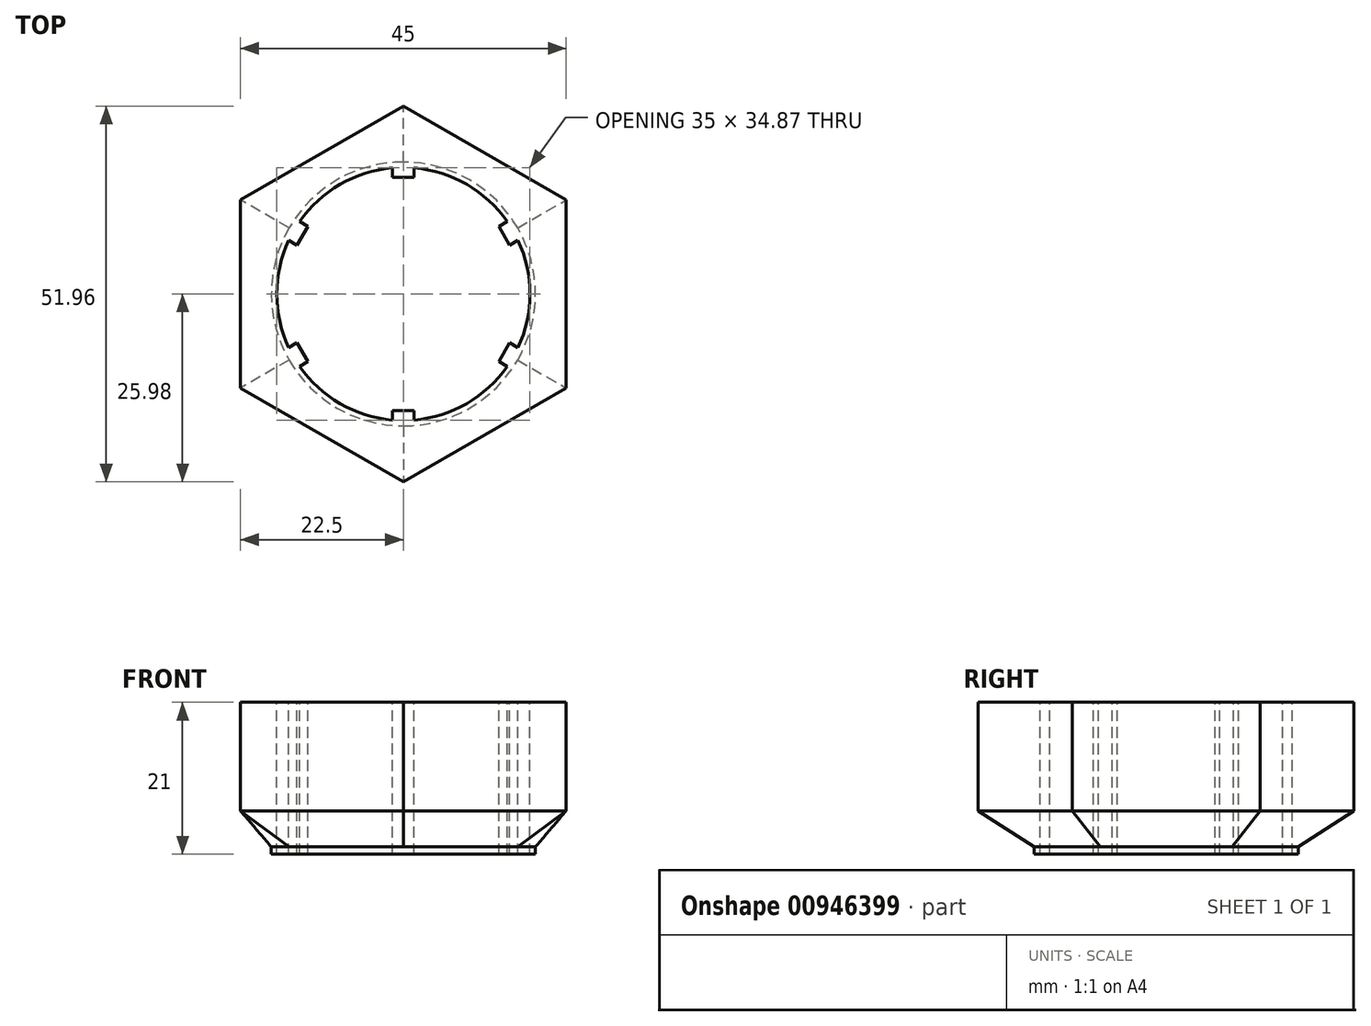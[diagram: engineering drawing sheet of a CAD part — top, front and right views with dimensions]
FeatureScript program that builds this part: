
annotation { "Feature Type Name" : "Feature", "Feature Type Description" : "" }
export const myFeature = defineFeature(function(context is Context, id is Id, definition is map)
    precondition{}
    {
        {
            var Q0;
            Q0=qCreatedBy(makeId("Top.planeOp"),FACE);
            var sketch = newSketch(context, id + "F0", { "sketchPlane" : qUnion([Q0])});
            skCircle(sketch, "E0", {"center": v(0, 0) * mm, "radius": 18.25 * mm});
            skArc(sketch, "E1", {"start": v(-15.85, 7.42) * mm, "mid": v(-17.5, 0) * mm, "end": v(-15.85, -7.42) * mm, "construction": true});
            skCircle(sketch, "E2", {"center": v(0, 0) * mm, "radius": 16.1 * mm, "construction": true});
            skLineSegment(sketch, "E3", {"start": v(0, 16.1) * mm, "end": v(0, 17.5) * mm, "construction": true});
            skLineSegment(sketch, "E4", {"start": v(-1.5, 16.1) * mm, "end": v(1.5, 16.1) * mm, "construction": true});
            skLineSegment(sketch, "E5", {"start": v(1.5, 16.1) * mm, "end": v(1.5, 17.44) * mm, "construction": true});
            skLineSegment(sketch, "E6", {"start": v(-1.5, 16.1) * mm, "end": v(-1.5, 17.44) * mm, "construction": true});
            skLineSegment(sketch, "E7.1.0", {"start": v(-14.7, 6.75) * mm, "end": v(-15.85, 7.42) * mm, "construction": true});
            skLineSegment(sketch, "E7.1.1", {"start": v(-13.2, 9.35) * mm, "end": v(-14.35, 10.02) * mm, "construction": true});
            skLineSegment(sketch, "E7.1.2", {"start": v(-14.7, 6.75) * mm, "end": v(-13.2, 9.35) * mm, "construction": true});
            skLineSegment(sketch, "E7.2.0", {"start": v(-13.2, -9.35) * mm, "end": v(-14.35, -10.02) * mm, "construction": true});
            skLineSegment(sketch, "E7.2.1", {"start": v(-14.7, -6.75) * mm, "end": v(-15.85, -7.42) * mm, "construction": true});
            skLineSegment(sketch, "E7.2.2", {"start": v(-13.2, -9.35) * mm, "end": v(-14.7, -6.75) * mm, "construction": true});
            skLineSegment(sketch, "E7.3.0", {"start": v(1.5, -16.1) * mm, "end": v(1.5, -17.44) * mm, "construction": true});
            skLineSegment(sketch, "E7.3.1", {"start": v(-1.5, -16.1) * mm, "end": v(-1.5, -17.44) * mm, "construction": true});
            skLineSegment(sketch, "E7.3.2", {"start": v(1.5, -16.1) * mm, "end": v(-1.5, -16.1) * mm, "construction": true});
            skLineSegment(sketch, "E7.4.0", {"start": v(14.7, -6.75) * mm, "end": v(15.85, -7.42) * mm, "construction": true});
            skLineSegment(sketch, "E7.4.1", {"start": v(13.2, -9.35) * mm, "end": v(14.35, -10.02) * mm, "construction": true});
            skLineSegment(sketch, "E7.4.2", {"start": v(14.7, -6.75) * mm, "end": v(13.2, -9.35) * mm, "construction": true});
            skLineSegment(sketch, "E7.5.0", {"start": v(13.2, 9.35) * mm, "end": v(14.35, 10.02) * mm, "construction": true});
            skLineSegment(sketch, "E7.5.1", {"start": v(14.7, 6.75) * mm, "end": v(15.85, 7.42) * mm, "construction": true});
            skLineSegment(sketch, "E7.5.2", {"start": v(13.2, 9.35) * mm, "end": v(14.7, 6.75) * mm, "construction": true});
            skArc(sketch, "E8.trimOffspring", {"start": v(14.35, 10.02) * mm, "mid": v(8.75, 15.16) * mm, "end": v(1.5, 17.44) * mm, "construction": true});
            skArc(sketch, "E9.trimOffspring", {"start": v(15.85, -7.42) * mm, "mid": v(17.5, 0) * mm, "end": v(15.85, 7.42) * mm, "construction": true});
            skArc(sketch, "E10.trimOffspring", {"start": v(1.5, -17.44) * mm, "mid": v(8.75, -15.16) * mm, "end": v(14.35, -10.02) * mm, "construction": true});
            skArc(sketch, "E11.trimOffspring", {"start": v(-14.35, -10.02) * mm, "mid": v(-8.75, -15.16) * mm, "end": v(-1.5, -17.44) * mm, "construction": true});
            skArc(sketch, "E12.trimOffspring", {"start": v(-1.5, 17.44) * mm, "mid": v(-8.75, 15.16) * mm, "end": v(-14.35, 10.02) * mm, "construction": true});
            skSolve(sketch);
        }
        {
            var Q0;
            Q0=qCreatedBy(makeId("Top.planeOp"),FACE);
            cPlane(context, id + "F1", {"entities" : qUnion([Q0]), "cplaneType" : CPlaneType.OFFSET, "offset" : 5 * mm, "width" : 150 * mm, "height" : 150 * mm});
        }
        {
            var Q0;
            Q0=qCreatedBy(id+"F1.planeOp",FACE);
            var sketch = newSketch(context, id + "F2", { "sketchPlane" : qUnion([Q0])});
            skCircle(sketch, "E13", {"center": v(0, 0) * mm, "radius": 22.5 * mm, "construction": true});
            skLineSegment(sketch, "E14", {"start": v(0, 25.98) * mm, "end": v(-22.5, 13) * mm});
            skLineSegment(sketch, "E15", {"start": v(-22.5, 13) * mm, "end": v(-22.5, -13) * mm});
            skLineSegment(sketch, "E16", {"start": v(-22.5, -13) * mm, "end": v(0, -25.98) * mm});
            skLineSegment(sketch, "E17", {"start": v(0, -25.98) * mm, "end": v(22.5, -13) * mm});
            skLineSegment(sketch, "E18", {"start": v(22.5, -13) * mm, "end": v(22.5, 13) * mm});
            skLineSegment(sketch, "E19", {"start": v(22.5, 13) * mm, "end": v(0, 25.98) * mm});
            skArc(sketch, "E20", {"start": v(-15.85, 7.42) * mm, "mid": v(-17.5, 0) * mm, "end": v(-15.85, -7.42) * mm, "construction": true});
            skCircle(sketch, "E21", {"center": v(0, 0) * mm, "radius": 16.1 * mm, "construction": true});
            skLineSegment(sketch, "E22", {"start": v(0, 16.1) * mm, "end": v(0, 17.5) * mm, "construction": true});
            skLineSegment(sketch, "E23", {"start": v(-1.5, 16.1) * mm, "end": v(1.5, 16.1) * mm, "construction": true});
            skLineSegment(sketch, "E24", {"start": v(1.5, 16.1) * mm, "end": v(1.5, 17.44) * mm, "construction": true});
            skLineSegment(sketch, "E25", {"start": v(-1.5, 16.1) * mm, "end": v(-1.5, 17.44) * mm, "construction": true});
            skLineSegment(sketch, "E26.1.0", {"start": v(-14.7, 6.75) * mm, "end": v(-15.85, 7.42) * mm, "construction": true});
            skLineSegment(sketch, "E26.1.1", {"start": v(-13.2, 9.35) * mm, "end": v(-14.35, 10.02) * mm, "construction": true});
            skLineSegment(sketch, "E26.1.2", {"start": v(-14.7, 6.75) * mm, "end": v(-13.2, 9.35) * mm, "construction": true});
            skLineSegment(sketch, "E26.2.0", {"start": v(-13.2, -9.35) * mm, "end": v(-14.35, -10.02) * mm, "construction": true});
            skLineSegment(sketch, "E26.2.1", {"start": v(-14.7, -6.75) * mm, "end": v(-15.85, -7.42) * mm, "construction": true});
            skLineSegment(sketch, "E26.2.2", {"start": v(-13.2, -9.35) * mm, "end": v(-14.7, -6.75) * mm, "construction": true});
            skLineSegment(sketch, "E26.3.0", {"start": v(1.5, -16.1) * mm, "end": v(1.5, -17.44) * mm, "construction": true});
            skLineSegment(sketch, "E26.3.1", {"start": v(-1.5, -16.1) * mm, "end": v(-1.5, -17.44) * mm, "construction": true});
            skLineSegment(sketch, "E26.3.2", {"start": v(1.5, -16.1) * mm, "end": v(-1.5, -16.1) * mm, "construction": true});
            skLineSegment(sketch, "E26.4.0", {"start": v(14.7, -6.75) * mm, "end": v(15.85, -7.42) * mm, "construction": true});
            skLineSegment(sketch, "E26.4.1", {"start": v(13.2, -9.35) * mm, "end": v(14.35, -10.02) * mm, "construction": true});
            skLineSegment(sketch, "E26.4.2", {"start": v(14.7, -6.75) * mm, "end": v(13.2, -9.35) * mm, "construction": true});
            skLineSegment(sketch, "E26.5.0", {"start": v(13.2, 9.35) * mm, "end": v(14.35, 10.02) * mm, "construction": true});
            skLineSegment(sketch, "E26.5.1", {"start": v(14.7, 6.75) * mm, "end": v(15.85, 7.42) * mm, "construction": true});
            skLineSegment(sketch, "E26.5.2", {"start": v(13.2, 9.35) * mm, "end": v(14.7, 6.75) * mm, "construction": true});
            skArc(sketch, "E27.trimOffspring", {"start": v(14.35, 10.02) * mm, "mid": v(8.75, 15.16) * mm, "end": v(1.5, 17.44) * mm, "construction": true});
            skArc(sketch, "E28.trimOffspring", {"start": v(15.85, -7.42) * mm, "mid": v(17.5, 0) * mm, "end": v(15.85, 7.42) * mm, "construction": true});
            skArc(sketch, "E29.trimOffspring", {"start": v(1.5, -17.44) * mm, "mid": v(8.75, -15.16) * mm, "end": v(14.35, -10.02) * mm, "construction": true});
            skArc(sketch, "E30.trimOffspring", {"start": v(-14.35, -10.02) * mm, "mid": v(-8.75, -15.16) * mm, "end": v(-1.5, -17.44) * mm, "construction": true});
            skArc(sketch, "E31.trimOffspring", {"start": v(-1.5, 17.44) * mm, "mid": v(-8.75, 15.16) * mm, "end": v(-14.35, 10.02) * mm, "construction": true});
            skSolve(sketch);
        }
        {
            var Q0;
            Q0=qCreatedBy(id+"F1.planeOp",FACE);
            var sketch = newSketch(context, id + "F3", { "sketchPlane" : qUnion([Q0])});
            skArc(sketch, "E32", {"start": v(-15.85, 7.42) * mm, "mid": v(-17.5, 0) * mm, "end": v(-15.85, -7.42) * mm});
            skCircle(sketch, "E33", {"center": v(0, 0) * mm, "radius": 16.1 * mm, "construction": true});
            skLineSegment(sketch, "E34", {"start": v(0, 16.1) * mm, "end": v(0, 17.5) * mm, "construction": true});
            skLineSegment(sketch, "E35", {"start": v(-1.5, 16.1) * mm, "end": v(1.5, 16.1) * mm});
            skLineSegment(sketch, "E36", {"start": v(1.5, 16.1) * mm, "end": v(1.5, 17.44) * mm});
            skLineSegment(sketch, "E37", {"start": v(-1.5, 16.1) * mm, "end": v(-1.5, 17.44) * mm});
            skLineSegment(sketch, "E38.1.0", {"start": v(-14.7, 6.75) * mm, "end": v(-15.85, 7.42) * mm});
            skLineSegment(sketch, "E38.1.1", {"start": v(-13.2, 9.35) * mm, "end": v(-14.35, 10.02) * mm});
            skLineSegment(sketch, "E38.1.2", {"start": v(-14.7, 6.75) * mm, "end": v(-13.2, 9.35) * mm});
            skLineSegment(sketch, "E38.2.0", {"start": v(-13.2, -9.35) * mm, "end": v(-14.35, -10.02) * mm});
            skLineSegment(sketch, "E38.2.1", {"start": v(-14.7, -6.75) * mm, "end": v(-15.85, -7.42) * mm});
            skLineSegment(sketch, "E38.2.2", {"start": v(-13.2, -9.35) * mm, "end": v(-14.7, -6.75) * mm});
            skLineSegment(sketch, "E38.3.0", {"start": v(1.5, -16.1) * mm, "end": v(1.5, -17.44) * mm});
            skLineSegment(sketch, "E38.3.1", {"start": v(-1.5, -16.1) * mm, "end": v(-1.5, -17.44) * mm});
            skLineSegment(sketch, "E38.3.2", {"start": v(1.5, -16.1) * mm, "end": v(-1.5, -16.1) * mm});
            skLineSegment(sketch, "E38.4.0", {"start": v(14.7, -6.75) * mm, "end": v(15.85, -7.42) * mm});
            skLineSegment(sketch, "E38.4.1", {"start": v(13.2, -9.35) * mm, "end": v(14.35, -10.02) * mm});
            skLineSegment(sketch, "E38.4.2", {"start": v(14.7, -6.75) * mm, "end": v(13.2, -9.35) * mm});
            skLineSegment(sketch, "E38.5.0", {"start": v(13.2, 9.35) * mm, "end": v(14.35, 10.02) * mm});
            skLineSegment(sketch, "E38.5.1", {"start": v(14.7, 6.75) * mm, "end": v(15.85, 7.42) * mm});
            skLineSegment(sketch, "E38.5.2", {"start": v(13.2, 9.35) * mm, "end": v(14.7, 6.75) * mm});
            skArc(sketch, "E39.trimOffspring", {"start": v(14.35, 10.02) * mm, "mid": v(8.75, 15.16) * mm, "end": v(1.5, 17.44) * mm});
            skArc(sketch, "E40.trimOffspring", {"start": v(15.85, -7.42) * mm, "mid": v(17.5, 0) * mm, "end": v(15.85, 7.42) * mm});
            skArc(sketch, "E41.trimOffspring", {"start": v(1.5, -17.44) * mm, "mid": v(8.75, -15.16) * mm, "end": v(14.35, -10.02) * mm});
            skArc(sketch, "E42.trimOffspring", {"start": v(-14.35, -10.02) * mm, "mid": v(-8.75, -15.16) * mm, "end": v(-1.5, -17.44) * mm});
            skArc(sketch, "E43.trimOffspring", {"start": v(-1.5, 17.44) * mm, "mid": v(-8.75, 15.16) * mm, "end": v(-14.35, 10.02) * mm});
            skSolve(sketch);
        }
        {
            var Q0;
            Q0 = qSketchRegion(id + "F0", true);
            var Q1;
            Q1 = qSketchRegion(id + "F2", true);
            loft(context, id + "F4", {"sheetProfilesArray" : [{ "sheetProfileEntities" : qUnion([Q0]) }, { "sheetProfileEntities" : qUnion([Q1]) }]});
        }
        {
            var Q0;
            Q0=makeQuery(id+"F4.opLoft","CAP_FACE",FACE,{"disambiguationData":[OSD([makeQuery(id+"F2.imprint","IMPRINT",FACE,{"disambiguationData":[TD([[makeQuery(id+"F2.imprint","IMPRINT",EDGE,{"derivedFrom":sQuery(id+"F2.wireOp",EDGE,"E14")}),1.0]])]})])],"isStart":true});
            extrude(context, id + "F5", {"entities" : qUnion([Q0]), "operationType" : NewBodyOperationType.ADD, "depth" : 15 * mm, "offsetDistance" : 25 * mm});
        }
        {
            var Q0;
            Q0 = qSketchRegion(id + "F3", true);
            extrude(context, id + "F6", {"entities" : qUnion([Q0]), "operationType" : NewBodyOperationType.REMOVE, "endBound" : BoundingType.THROUGH_ALL, "oppositeDirection" : true, "depth" : 25 * mm, "offsetDistance" : 25 * mm});
        }
        {
            var Q0;
            Q0 = qSketchRegion(id + "F3", true);
            extrude(context, id + "F7", {"entities" : qUnion([Q0]), "operationType" : NewBodyOperationType.REMOVE, "depth" : 25 * mm, "offsetDistance" : 25 * mm});
        }
        {
            var Q0;
            Q0=makeQuery(id+"F4.opLoft","CAP_FACE",FACE,{"disambiguationData":[OSD([makeQuery(id+"F0.imprint","IMPRINT",FACE,{"disambiguationData":[TD([[makeQuery(id+"F0.imprint","IMPRINT",EDGE,{"derivedFrom":sQuery(id+"F0.wireOp",EDGE,"E0")}),1.0]])]})])],"isStart":true});
            extrude(context, id + "F8", {"entities" : qUnion([Q0]), "operationType" : NewBodyOperationType.ADD, "depth" : 1 * mm, "offsetDistance" : 25 * mm});
        }
    });
